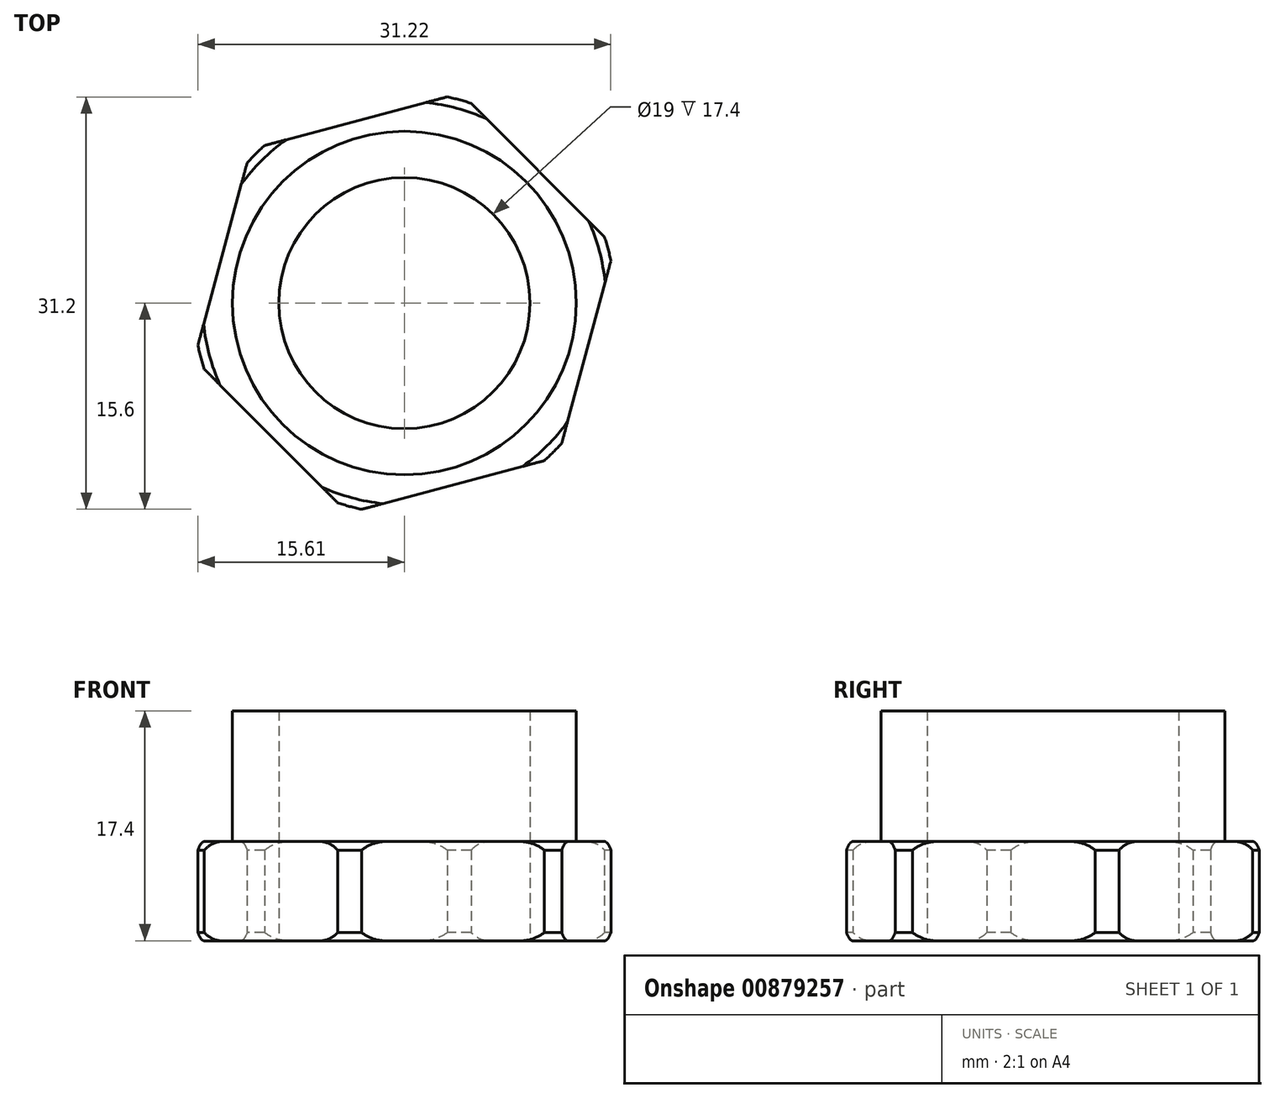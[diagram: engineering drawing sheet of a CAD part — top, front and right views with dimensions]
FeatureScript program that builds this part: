
annotation { "Feature Type Name" : "Feature", "Feature Type Description" : "" }
export const myFeature = defineFeature(function(context is Context, id is Id, definition is map)
    precondition{}
    {
        {
            var Q0;
            Q0=qCreatedBy(makeId("Top.planeOp"),FACE);
            var sketch = newSketch(context, id + "F0", { "sketchPlane" : qUnion([Q0])});
            skCircle(sketch, "E0", {"center": v(0, 0) * mm, "radius": 13 * mm});
            skCircle(sketch, "E1", {"center": v(0, 0) * mm, "radius": 9.5 * mm});
            skSolve(sketch);
        }
        {
            var Q0;
            Q0 = qSketchRegion(id + "F0", true);
            extrude(context, id + "F1", {"entities" : qUnion([Q0]), "depth" : 17.4 * mm, "offsetDistance" : 25 * mm});
        }
        {
            var Q0;
            Q0=qCreatedBy(makeId("Top.planeOp"),FACE);
            var sketch = newSketch(context, id + "F2", { "sketchPlane" : qUnion([Q0])});
            skCircle(sketch, "E2", {"center": v(0, 0) * mm, "radius": 14.2 * mm});
            skSolve(sketch);
        }
        {
            var Q0;
            Q0=makeQuery(id+"F2.imprint","IMPRINT",FACE,{"disambiguationData":[TD([[makeQuery(id+"F2.imprint","IMPRINT",EDGE,{"derivedFrom":sQuery(id+"F2.wireOp",EDGE,"E2")}),1.0]])]});
            var sketch = newSketch(context, id + "F3", { "sketchPlane" : qUnion([Q0])});
            skCircle(sketch, "E3.cCircle", {"center": v(0, 0) * mm, "radius": 14.25 * mm, "construction": true});
            skLineSegment(sketch, "E3.0", {"start": v(15.9, 4.24) * mm, "end": v(11.62, -11.65) * mm});
            skLineSegment(sketch, "E3.1", {"start": v(11.62, -11.65) * mm, "end": v(-4.28, -15.88) * mm});
            skLineSegment(sketch, "E3.2", {"start": v(-4.28, -15.88) * mm, "end": v(-15.9, -4.24) * mm});
            skLineSegment(sketch, "E3.3", {"start": v(-15.9, -4.24) * mm, "end": v(-11.62, 11.65) * mm});
            skLineSegment(sketch, "E3.4", {"start": v(-11.62, 11.65) * mm, "end": v(4.28, 15.88) * mm});
            skLineSegment(sketch, "E3.5", {"start": v(4.28, 15.88) * mm, "end": v(15.9, 4.24) * mm});
            skPoint(sketch, "E3.0.midPoint", {"position": v(13.76, -3.7) * mm});
            skSolve(sketch);
        }
        {
            var Q0;
            Q0=makeQuery(id+"F2.imprint","IMPRINT",FACE,{"disambiguationData":[TD([[makeQuery(id+"F2.imprint","IMPRINT",EDGE,{"derivedFrom":sQuery(id+"F2.wireOp",EDGE,"E2")}),1.0]])]});
            var Q1;
            Q1=makeQuery(id+"F3.imprint","IMPRINT",FACE,{"disambiguationData":[TD([[makeQuery(id+"F3.imprint","IMPRINT",EDGE,{"derivedFrom":sQuery(id+"F3.wireOp",EDGE,"E3.0")}),-1.0]])]});
            extrude(context, id + "F4", {"entities" : qUnion([Q0, Q1]), "operationType" : NewBodyOperationType.ADD, "depth" : 7.5 * mm, "offsetDistance" : 25 * mm});
        }
        {
            var Q0;
            Q0=makeQuery(id+"F2.imprint","IMPRINT",FACE,{"disambiguationData":[TD([[makeQuery(id+"F2.imprint","IMPRINT",EDGE,{"derivedFrom":sQuery(id+"F2.wireOp",EDGE,"E2")}),1.0]])]});
            var sketch = newSketch(context, id + "F5", { "sketchPlane" : qUnion([Q0])});
            skCircle(sketch, "E4.0.0", {"center": v(0, 0) * mm, "radius": 14.2 * mm});
            skCircle(sketch, "E5.0", {"center": v(0, 0) * mm, "radius": 9.5 * mm});
            skSolve(sketch);
        }
        {
            var Q0;
            Q0=makeQuery(id+"F5.imprint","IMPRINT",FACE,{"disambiguationData":[TD([[makeQuery(id+"F5.imprint","IMPRINT",EDGE,{"derivedFrom":sQuery(id+"F5.wireOp",EDGE,"E5.0")}),1.0]])]});
            extrude(context, id + "F6", {"entities" : qUnion([Q0]), "operationType" : NewBodyOperationType.REMOVE, "depth" : 25 * mm, "offsetDistance" : 25 * mm});
        }
        {
            var Q0;
            Q0=makeQuery(id+"F4.opExtrude","SWEPT_FACE",FACE,{"disambiguationData":[OSD([sQuery(id+"F3.wireOp",EDGE,"E3.2")])]});
            var sketch = newSketch(context, id + "F7", { "sketchPlane" : qUnion([Q0])});
            skArc(sketch, "E6", {"start": v(-8.23, 2.28) * mm, "mid": v(-7.08, 0.57) * mm, "end": v(-5.1, 0) * mm});
            skArc(sketch, "E7", {"start": v(-5.07, 7.5) * mm, "mid": v(-7.11, 6.87) * mm, "end": v(-8.23, 5.05) * mm});
            skSolve(sketch);
        }
        {
            var Q0;
            {var subQ0=sQuery(id+"F7.wireOp",EDGE,"E6");var subQ1=sQuery(id+"F3.wireOp",EDGE,"E3.2");var subQ4=makeQuery(id+"F4.opExtrude","CAP_EDGE",EDGE,{"disambiguationData":[OSD([subQ1])],"isStart":true});var subQ5=makeQuery(id+"F7.imprint","INTERSECT",VERTEX,{"disambiguationData":[OD(1.0)],"derivedFrom":[subQ4,subQ0]});Q0=makeQuery(id+"F7.imprint","IMPRINT",FACE,{"disambiguationData":[TD([[makeQuery(id+"F7.imprint","IMPRINT",EDGE,{"disambiguationData":[TD([[subQ5,1.0]])],"derivedFrom":subQ0}),-1.0]])]});}
            var Q1;
            {var subQ0=sQuery(id+"F7.wireOp",EDGE,"E7");var subQ1=sQuery(id+"F3.wireOp",EDGE,"E3.2");var subQ4=makeQuery(id+"F4.opExtrude","CAP_EDGE",EDGE,{"disambiguationData":[OSD([subQ1])],"isStart":false});var subQ5=makeQuery(id+"F7.imprint","INTERSECT",VERTEX,{"disambiguationData":[OD(1.0)],"derivedFrom":[subQ4,subQ0]});Q1=makeQuery(id+"F7.imprint","IMPRINT",FACE,{"disambiguationData":[TD([[makeQuery(id+"F7.imprint","IMPRINT",EDGE,{"disambiguationData":[TD([[subQ5,-1.0]])],"derivedFrom":subQ0}),-1.0]])]});}
            var Q2;
            Q2=makeQuery(id+"F6.boolean.opBoolean","MERGE",FACE,{"derivedFrom":[makeQuery(id+"F1.opExtrude","SWEPT_FACE",FACE,{"disambiguationData":[OSD([sQuery(id+"F0.wireOp",EDGE,"E1")])]})],"fromTools":[makeQuery(id+"F6.opExtrude","SWEPT_FACE",FACE,{"disambiguationData":[OSD([sQuery(id+"F5.wireOp",EDGE,"E5.0")])]})]});
            revolve(context, id + "F8", {"operationType" : NewBodyOperationType.REMOVE, "surfaceOperationType" : NewSurfaceOperationType.NEW, "entities" : qUnion([Q0, Q1]), "axis" : qUnion([Q2]), "revolveType" : RevolveType.FULL, "oppositeDirection" : true});
        }
        {
            var Q0;
            {var subQ0=sQuery(id+"F2.wireOp",EDGE,"E2");Q0=makeQuery(id+"F4.boolean.opBoolean","MERGE",FACE,{"derivedFrom":[makeQuery(id+"F1.opExtrude","CAP_FACE",FACE,{"disambiguationData":[OSD([sQuery(id+"F0.wireOp",EDGE,"E0"),sQuery(id+"F0.wireOp",EDGE,"E1")])],"isStart":true}),makeQuery(id+"F4.opExtrude","CAP_FACE",FACE,{"disambiguationData":[OSD([subQ0])],"isStart":true}),makeQuery(id+"F4.opExtrude","CAP_FACE",FACE,{"disambiguationData":[OSD([subQ0,sQuery(id+"F3.wireOp",EDGE,"E3.0"),sQuery(id+"F3.wireOp",EDGE,"E3.1"),sQuery(id+"F3.wireOp",EDGE,"E3.2"),sQuery(id+"F3.wireOp",EDGE,"E3.3"),sQuery(id+"F3.wireOp",EDGE,"E3.4"),sQuery(id+"F3.wireOp",EDGE,"E3.5")])],"isStart":true})]});}
            var sketch = newSketch(context, id + "F9", { "sketchPlane" : qUnion([Q0])});
            skCircle(sketch, "E8", {"center": v(0, 0) * mm, "radius": 15.94 * mm});
            skCircle(sketch, "E9", {"center": v(0, 0) * mm, "radius": 16.7 * mm});
            skSolve(sketch);
        }
        {
            var Q0;
            Q0 = qSketchRegion(id + "F9", true);
            extrude(context, id + "F10", {"entities" : qUnion([Q0]), "operationType" : NewBodyOperationType.REMOVE, "oppositeDirection" : true, "depth" : 25 * mm, "offsetDistance" : 25 * mm});
        }
    });
